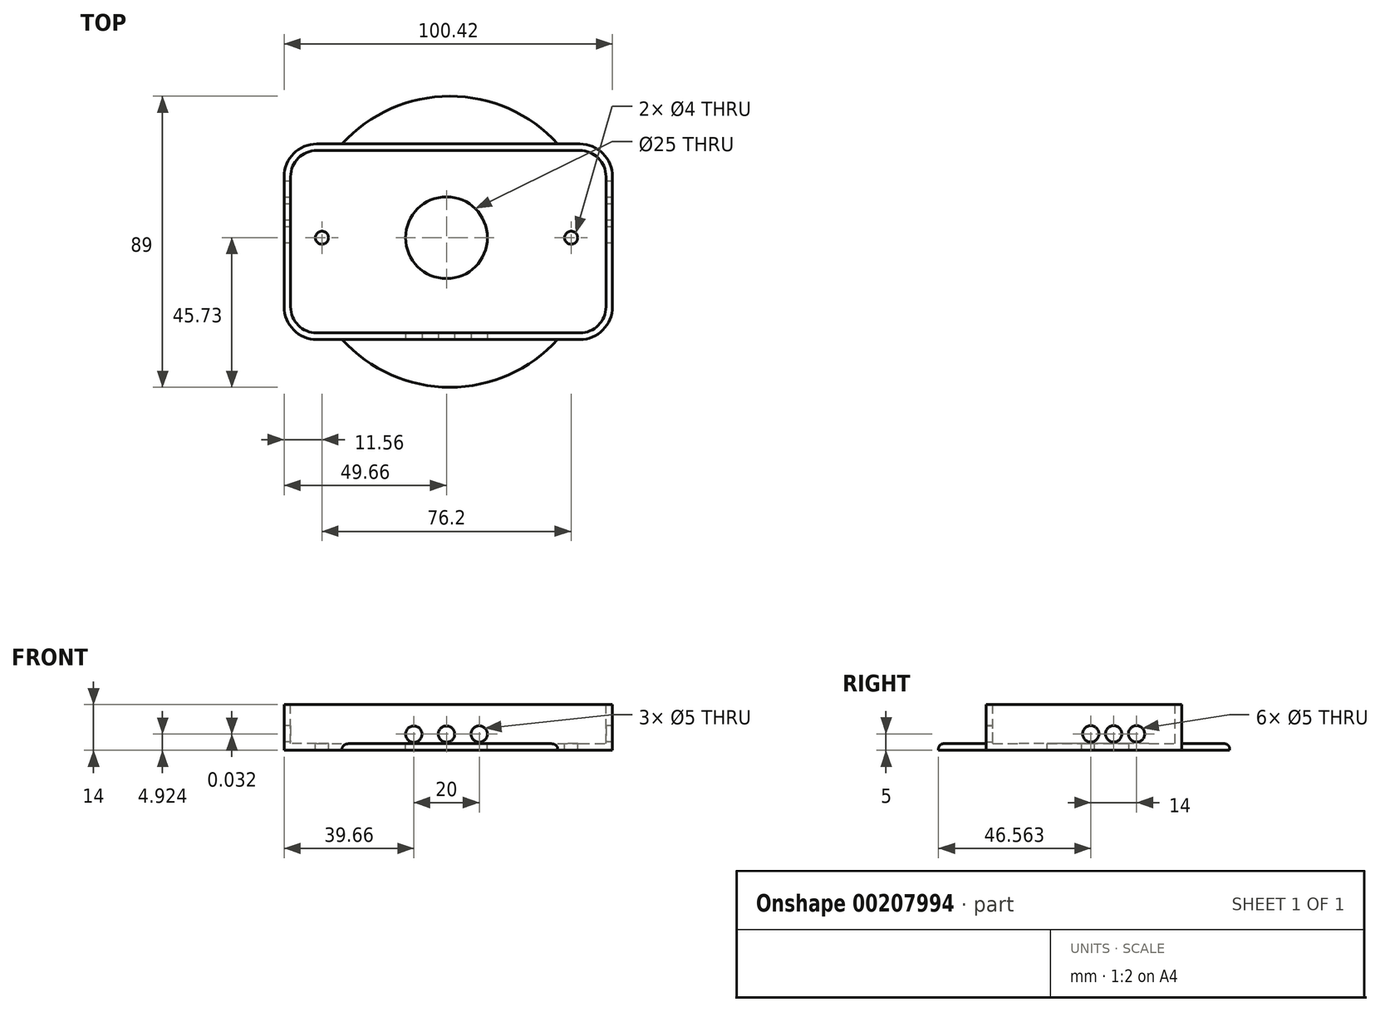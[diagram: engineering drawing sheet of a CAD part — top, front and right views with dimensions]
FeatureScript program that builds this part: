
annotation { "Feature Type Name" : "Feature", "Feature Type Description" : "" }
export const myFeature = defineFeature(function(context is Context, id is Id, definition is map)
    precondition{}
    {
        {
            var Q0;
            Q0=qCreatedBy(makeId("Top.planeOp"),FACE);
            var sketch = newSketch(context, id + "F0", { "sketchPlane" : qUnion([Q0])});
            skCircle(sketch, "E0", {"center": v(-41.26, 20.47) * mm, "radius": 3.2 * mm});
            skCircle(sketch, "E1", {"center": v(37.34, 20.47) * mm, "radius": 3.2 * mm});
            skCircle(sketch, "E2", {"center": v(37.34, -22.93) * mm, "radius": 3.2 * mm});
            skCircle(sketch, "E3", {"center": v(-41.26, -22.93) * mm, "radius": 3.2 * mm});
            skLineSegment(sketch, "E4.bottom", {"start": v(-44.46, 23.67) * mm, "end": v(40.54, 23.67) * mm});
            skLineSegment(sketch, "E4.top", {"start": v(-44.46, -26.13) * mm, "end": v(40.54, -26.13) * mm});
            skLineSegment(sketch, "E4.left", {"start": v(-44.46, 23.67) * mm, "end": v(-44.46, -26.13) * mm});
            skLineSegment(sketch, "E4.right", {"start": v(40.54, 23.67) * mm, "end": v(40.54, -26.13) * mm});
            skLineSegment(sketch, "E5.bottom", {"start": v(-28.76, 21.37) * mm, "end": v(30.84, 21.37) * mm});
            skLineSegment(sketch, "E5.top", {"start": v(-28.76, -23.83) * mm, "end": v(30.84, -23.83) * mm});
            skLineSegment(sketch, "E5.left", {"start": v(-28.76, 21.37) * mm, "end": v(-28.76, -23.83) * mm});
            skLineSegment(sketch, "E5.right", {"start": v(30.84, 21.37) * mm, "end": v(30.84, -23.83) * mm});
            skLineSegment(sketch, "E6.bottom", {"start": v(-39.66, 28.67) * mm, "end": v(40.76, 28.67) * mm});
            skLineSegment(sketch, "E6.top", {"start": v(-39.66, -31.13) * mm, "end": v(40.76, -31.13) * mm});
            skLineSegment(sketch, "E6.left", {"start": v(-49.66, 18.67) * mm, "end": v(-49.66, -21.13) * mm});
            skLineSegment(sketch, "E6.right", {"start": v(50.76, 18.67) * mm, "end": v(50.76, -21.13) * mm});
            skCircle(sketch, "E7", {"center": v(1.04, -1.23) * mm, "radius": 44.5 * mm});
            skPoint(sketch, "E7.centerSnap0", {"position": v(1.04, -23.83) * mm});
            skPoint(sketch, "E7.centerSnap1", {"position": v(-28.76, -1.23) * mm});
            skPoint(sketch, "E8.visualSharp", {"position": v(50.76, 28.67) * mm});
            skArc(sketch, "E8.filletArc", {"start": v(50.76, 18.67) * mm, "mid": v(47.83, 25.74) * mm, "end": v(40.76, 28.67) * mm});
            skPoint(sketch, "E9.visualSharp", {"position": v(-49.66, 28.67) * mm});
            skArc(sketch, "E9.filletArc", {"start": v(-39.66, 28.67) * mm, "mid": v(-46.74, 25.74) * mm, "end": v(-49.66, 18.67) * mm});
            skPoint(sketch, "E10.visualSharp", {"position": v(-49.66, -31.13) * mm});
            skArc(sketch, "E10.filletArc", {"start": v(-49.66, -21.13) * mm, "mid": v(-46.74, -28.2) * mm, "end": v(-39.66, -31.13) * mm});
            skPoint(sketch, "E11.visualSharp", {"position": v(50.76, -31.13) * mm});
            skArc(sketch, "E11.filletArc", {"start": v(40.76, -31.13) * mm, "mid": v(47.83, -28.2) * mm, "end": v(50.76, -21.13) * mm});
            skSolve(sketch);
        }
        {
            var Q0;
            {var subQ1=sQuery(id+"F0.wireOp",EDGE,"E4.bottom");var subQ13=sQuery(id+"F0.wireOp",EDGE,"E0");var subQ20=makeQuery(id+"F0.imprint","INTERSECT",VERTEX,{"disambiguationData":[OD(1.0)],"derivedFrom":[subQ13,subQ1]});Q0=makeQuery(id+"F0.imprint","IMPRINT",FACE,{"disambiguationData":[TD([[makeQuery(id+"F0.imprint","IMPRINT",EDGE,{"disambiguationData":[TD([[subQ20,1.0]])],"derivedFrom":subQ13}),-1.0]])]});}
            var Q1;
            {var subQ0=sQuery(id+"F0.wireOp",EDGE,"E7");var subQ7=sQuery(id+"F0.wireOp",EDGE,"E5.bottom");var subQ12=makeQuery(id+"F0.imprint","INTERSECT",VERTEX,{"disambiguationData":[OD(0.0)],"derivedFrom":[subQ7,subQ0]});Q1=makeQuery(id+"F0.imprint","IMPRINT",FACE,{"disambiguationData":[TD([[makeQuery(id+"F0.imprint","IMPRINT",EDGE,{"disambiguationData":[TD([[subQ12,-1.0]])],"derivedFrom":subQ7}),-1.0]])]});}
            var Q2;
            {var subQ0=sQuery(id+"F0.wireOp",EDGE,"E4.bottom");var subQ1=sQuery(id+"F0.wireOp",EDGE,"E1");var subQ2=makeQuery(id+"F0.imprint","INTERSECT",VERTEX,{"disambiguationData":[OD(0.0)],"derivedFrom":[subQ1,subQ0]});Q2=makeQuery(id+"F0.imprint","IMPRINT",FACE,{"disambiguationData":[TD([[makeQuery(id+"F0.imprint","IMPRINT",EDGE,{"disambiguationData":[TD([[subQ2,1.0]])],"derivedFrom":subQ1}),1.0]])]});}
            var Q3;
            {var subQ0=sQuery(id+"F0.wireOp",EDGE,"E4.left");var subQ1=sQuery(id+"F0.wireOp",EDGE,"E3");var subQ2=makeQuery(id+"F0.imprint","INTERSECT",VERTEX,{"disambiguationData":[OD(0.0)],"derivedFrom":[subQ1,subQ0]});Q3=makeQuery(id+"F0.imprint","IMPRINT",FACE,{"disambiguationData":[TD([[makeQuery(id+"F0.imprint","IMPRINT",EDGE,{"disambiguationData":[TD([[subQ2,-1.0]])],"derivedFrom":subQ1}),1.0]])]});}
            var Q4;
            {var subQ0=sQuery(id+"F0.wireOp",EDGE,"E7");var subQ1=sQuery(id+"F0.wireOp",EDGE,"E4.top");var subQ2=makeQuery(id+"F0.imprint","INTERSECT",VERTEX,{"disambiguationData":[OD(0.0)],"derivedFrom":[subQ1,subQ0]});Q4=makeQuery(id+"F0.imprint","IMPRINT",FACE,{"disambiguationData":[TD([[makeQuery(id+"F0.imprint","IMPRINT",EDGE,{"disambiguationData":[TD([[subQ2,-1.0]])],"derivedFrom":subQ1}),-1.0]])]});}
            var Q5;
            {var subQ0=sQuery(id+"F0.wireOp",EDGE,"E7");var subQ1=sQuery(id+"F0.wireOp",EDGE,"E4.top");var subQ2=makeQuery(id+"F0.imprint","INTERSECT",VERTEX,{"disambiguationData":[OD(0.0)],"derivedFrom":[subQ1,subQ0]});Q5=makeQuery(id+"F0.imprint","IMPRINT",FACE,{"disambiguationData":[TD([[makeQuery(id+"F0.imprint","IMPRINT",EDGE,{"disambiguationData":[TD([[subQ2,-1.0]])],"derivedFrom":subQ1}),1.0]])]});}
            var Q6;
            {var subQ0=sQuery(id+"F0.wireOp",EDGE,"E7");var subQ1=sQuery(id+"F0.wireOp",EDGE,"E6.top");var subQ2=makeQuery(id+"F0.imprint","INTERSECT",VERTEX,{"disambiguationData":[OD(0.0)],"derivedFrom":[subQ1,subQ0]});Q6=makeQuery(id+"F0.imprint","IMPRINT",FACE,{"disambiguationData":[TD([[makeQuery(id+"F0.imprint","IMPRINT",EDGE,{"disambiguationData":[TD([[subQ2,-1.0]])],"derivedFrom":subQ1}),-1.0]])]});}
            var Q7;
            {var subQ0=sQuery(id+"F0.wireOp",EDGE,"E7");var subQ1=sQuery(id+"F0.wireOp",EDGE,"E6.bottom");var subQ2=makeQuery(id+"F0.imprint","INTERSECT",VERTEX,{"disambiguationData":[OD(0.0)],"derivedFrom":[subQ1,subQ0]});Q7=makeQuery(id+"F0.imprint","IMPRINT",FACE,{"disambiguationData":[TD([[makeQuery(id+"F0.imprint","IMPRINT",EDGE,{"disambiguationData":[TD([[subQ2,-1.0]])],"derivedFrom":subQ1}),1.0]])]});}
            var Q8;
            Q8=makeQuery(id+"F0.imprint","IMPRINT",FACE,{"disambiguationData":[TD([[makeQuery(id+"F0.imprint","IMPRINT",EDGE,{"derivedFrom":sQuery(id+"F0.wireOp",EDGE,"E6.right")}),-1.0]])]});
            var Q9;
            {var subQ1=sQuery(id+"F0.wireOp",EDGE,"E4.bottom");var subQ5=sQuery(id+"F0.wireOp",EDGE,"E1");var subQ6=makeQuery(id+"F0.imprint","INTERSECT",VERTEX,{"disambiguationData":[OD(1.0)],"derivedFrom":[subQ5,subQ1]});Q9=makeQuery(id+"F0.imprint","IMPRINT",FACE,{"disambiguationData":[TD([[makeQuery(id+"F0.imprint","IMPRINT",EDGE,{"disambiguationData":[TD([[subQ6,-1.0]])],"derivedFrom":subQ5}),-1.0]])]});}
            var Q10;
            {var subQ0=sQuery(id+"F0.wireOp",EDGE,"E4.bottom");var subQ1=sQuery(id+"F0.wireOp",EDGE,"E0");var subQ2=makeQuery(id+"F0.imprint","INTERSECT",VERTEX,{"disambiguationData":[OD(0.0)],"derivedFrom":[subQ1,subQ0]});Q10=makeQuery(id+"F0.imprint","IMPRINT",FACE,{"disambiguationData":[TD([[makeQuery(id+"F0.imprint","IMPRINT",EDGE,{"disambiguationData":[TD([[subQ2,-1.0]])],"derivedFrom":subQ1}),1.0]])]});}
            var Q11;
            {var subQ0=sQuery(id+"F0.wireOp",EDGE,"E7");var subQ1=sQuery(id+"F0.wireOp",EDGE,"E4.bottom");var subQ2=makeQuery(id+"F0.imprint","INTERSECT",VERTEX,{"disambiguationData":[OD(0.0)],"derivedFrom":[subQ1,subQ0]});Q11=makeQuery(id+"F0.imprint","IMPRINT",FACE,{"disambiguationData":[TD([[makeQuery(id+"F0.imprint","IMPRINT",EDGE,{"disambiguationData":[TD([[subQ2,-1.0]])],"derivedFrom":subQ1}),-1.0]])]});}
            var Q12;
            {var subQ0=sQuery(id+"F0.wireOp",EDGE,"E7");var subQ1=sQuery(id+"F0.wireOp",EDGE,"E5.left");var subQ2=makeQuery(id+"F0.imprint","INTERSECT",VERTEX,{"disambiguationData":[OD(0.0)],"derivedFrom":[subQ1,subQ0]});Q12=makeQuery(id+"F0.imprint","IMPRINT",FACE,{"disambiguationData":[TD([[makeQuery(id+"F0.imprint","IMPRINT",EDGE,{"disambiguationData":[TD([[subQ2,-1.0]])],"derivedFrom":subQ1}),-1.0]])]});}
            var Q13;
            Q13=makeQuery(id+"F0.imprint","IMPRINT",FACE,{"disambiguationData":[TD([[makeQuery(id+"F0.imprint","IMPRINT",EDGE,{"derivedFrom":sQuery(id+"F0.wireOp",EDGE,"E6.left")}),1.0]])]});
            var Q14;
            {var subQ0=sQuery(id+"F0.wireOp",EDGE,"E4.top");var subQ1=sQuery(id+"F0.wireOp",EDGE,"E2");var subQ2=makeQuery(id+"F0.imprint","INTERSECT",VERTEX,{"disambiguationData":[OD(0.0)],"derivedFrom":[subQ1,subQ0]});Q14=makeQuery(id+"F0.imprint","IMPRINT",FACE,{"disambiguationData":[TD([[makeQuery(id+"F0.imprint","IMPRINT",EDGE,{"disambiguationData":[TD([[subQ2,1.0]])],"derivedFrom":subQ1}),1.0]])]});}
            var Q15;
            {var subQ0=sQuery(id+"F0.wireOp",EDGE,"E7");var subQ1=sQuery(id+"F0.wireOp",EDGE,"E5.right");var subQ2=makeQuery(id+"F0.imprint","INTERSECT",VERTEX,{"disambiguationData":[OD(0.0)],"derivedFrom":[subQ1,subQ0]});Q15=makeQuery(id+"F0.imprint","IMPRINT",FACE,{"disambiguationData":[TD([[makeQuery(id+"F0.imprint","IMPRINT",EDGE,{"disambiguationData":[TD([[subQ2,-1.0]])],"derivedFrom":subQ1}),1.0]])]});}
            var Q16;
            {var subQ0=sQuery(id+"F0.wireOp",EDGE,"E7");var subQ1=sQuery(id+"F0.wireOp",EDGE,"E4.bottom");var subQ2=makeQuery(id+"F0.imprint","INTERSECT",VERTEX,{"disambiguationData":[OD(0.0)],"derivedFrom":[subQ1,subQ0]});Q16=makeQuery(id+"F0.imprint","IMPRINT",FACE,{"disambiguationData":[TD([[makeQuery(id+"F0.imprint","IMPRINT",EDGE,{"disambiguationData":[TD([[subQ2,-1.0]])],"derivedFrom":subQ1}),1.0]])]});}
            var Q17;
            {var subQ0=sQuery(id+"F0.wireOp",EDGE,"E5.right");var subQ1=sQuery(id+"F0.wireOp",EDGE,"E5.top");var subQ2=makeQuery(id+"F0.imprint","INTERSECT",VERTEX,{"derivedFrom":[subQ1,subQ0]});Q17=makeQuery(id+"F0.imprint","IMPRINT",FACE,{"disambiguationData":[TD([[makeQuery(id+"F0.imprint","IMPRINT",EDGE,{"disambiguationData":[TD([[subQ2,1.0]])],"derivedFrom":subQ1}),1.0]])]});}
            var Q18;
            {var subQ0=sQuery(id+"F0.wireOp",EDGE,"E4.left");var subQ1=sQuery(id+"F0.wireOp",EDGE,"E3");var subQ2=makeQuery(id+"F0.imprint","INTERSECT",VERTEX,{"disambiguationData":[OD(0.0)],"derivedFrom":[subQ1,subQ0]});Q18=makeQuery(id+"F0.imprint","IMPRINT",FACE,{"disambiguationData":[TD([[makeQuery(id+"F0.imprint","IMPRINT",EDGE,{"disambiguationData":[TD([[subQ2,1.0]])],"derivedFrom":subQ1}),1.0]])]});}
            var Q19;
            {var subQ0=sQuery(id+"F0.wireOp",EDGE,"E4.left");var subQ1=sQuery(id+"F0.wireOp",EDGE,"E3");var subQ2=makeQuery(id+"F0.imprint","INTERSECT",VERTEX,{"disambiguationData":[OD(0.0)],"derivedFrom":[subQ1,subQ0]});Q19=makeQuery(id+"F0.imprint","IMPRINT",FACE,{"disambiguationData":[TD([[makeQuery(id+"F0.imprint","IMPRINT",EDGE,{"disambiguationData":[TD([[subQ2,-1.0]])],"derivedFrom":subQ1}),-1.0]])]});}
            var Q20;
            {var subQ0=sQuery(id+"F0.wireOp",EDGE,"E4.right");var subQ1=sQuery(id+"F0.wireOp",EDGE,"E2");var subQ2=makeQuery(id+"F0.imprint","INTERSECT",VERTEX,{"disambiguationData":[OD(0.0)],"derivedFrom":[subQ1,subQ0]});Q20=makeQuery(id+"F0.imprint","IMPRINT",FACE,{"disambiguationData":[TD([[makeQuery(id+"F0.imprint","IMPRINT",EDGE,{"disambiguationData":[TD([[subQ2,1.0]])],"derivedFrom":subQ1}),1.0]])]});}
            var Q21;
            {var subQ0=sQuery(id+"F0.wireOp",EDGE,"E4.top");var subQ1=sQuery(id+"F0.wireOp",EDGE,"E2");var subQ2=makeQuery(id+"F0.imprint","INTERSECT",VERTEX,{"disambiguationData":[OD(1.0)],"derivedFrom":[subQ1,subQ0]});Q21=makeQuery(id+"F0.imprint","IMPRINT",FACE,{"disambiguationData":[TD([[makeQuery(id+"F0.imprint","IMPRINT",EDGE,{"disambiguationData":[TD([[subQ2,-1.0]])],"derivedFrom":subQ1}),-1.0]])]});}
            var Q22;
            {var subQ0=sQuery(id+"F0.wireOp",EDGE,"E4.top");var subQ1=sQuery(id+"F0.wireOp",EDGE,"E2");var subQ2=makeQuery(id+"F0.imprint","INTERSECT",VERTEX,{"disambiguationData":[OD(0.0)],"derivedFrom":[subQ1,subQ0]});Q22=makeQuery(id+"F0.imprint","IMPRINT",FACE,{"disambiguationData":[TD([[makeQuery(id+"F0.imprint","IMPRINT",EDGE,{"disambiguationData":[TD([[subQ2,-1.0]])],"derivedFrom":subQ1}),1.0]])]});}
            var Q23;
            {var subQ0=sQuery(id+"F0.wireOp",EDGE,"E4.bottom");var subQ1=sQuery(id+"F0.wireOp",EDGE,"E1");var subQ2=makeQuery(id+"F0.imprint","INTERSECT",VERTEX,{"disambiguationData":[OD(0.0)],"derivedFrom":[subQ1,subQ0]});Q23=makeQuery(id+"F0.imprint","IMPRINT",FACE,{"disambiguationData":[TD([[makeQuery(id+"F0.imprint","IMPRINT",EDGE,{"disambiguationData":[TD([[subQ2,-1.0]])],"derivedFrom":subQ1}),1.0]])]});}
            var Q24;
            {var subQ0=sQuery(id+"F0.wireOp",EDGE,"E4.right");var subQ1=sQuery(id+"F0.wireOp",EDGE,"E1");var subQ2=makeQuery(id+"F0.imprint","INTERSECT",VERTEX,{"disambiguationData":[OD(0.0)],"derivedFrom":[subQ1,subQ0]});Q24=makeQuery(id+"F0.imprint","IMPRINT",FACE,{"disambiguationData":[TD([[makeQuery(id+"F0.imprint","IMPRINT",EDGE,{"disambiguationData":[TD([[subQ2,1.0]])],"derivedFrom":subQ1}),1.0]])]});}
            var Q25;
            {var subQ0=sQuery(id+"F0.wireOp",EDGE,"E4.bottom");var subQ1=sQuery(id+"F0.wireOp",EDGE,"E1");var subQ2=makeQuery(id+"F0.imprint","INTERSECT",VERTEX,{"disambiguationData":[OD(0.0)],"derivedFrom":[subQ1,subQ0]});Q25=makeQuery(id+"F0.imprint","IMPRINT",FACE,{"disambiguationData":[TD([[makeQuery(id+"F0.imprint","IMPRINT",EDGE,{"disambiguationData":[TD([[subQ2,1.0]])],"derivedFrom":subQ1}),-1.0]])]});}
            var Q26;
            {var subQ0=sQuery(id+"F0.wireOp",EDGE,"E4.left");var subQ1=sQuery(id+"F0.wireOp",EDGE,"E0");var subQ2=makeQuery(id+"F0.imprint","INTERSECT",VERTEX,{"disambiguationData":[OD(0.0)],"derivedFrom":[subQ1,subQ0]});Q26=makeQuery(id+"F0.imprint","IMPRINT",FACE,{"disambiguationData":[TD([[makeQuery(id+"F0.imprint","IMPRINT",EDGE,{"disambiguationData":[TD([[subQ2,-1.0]])],"derivedFrom":subQ1}),1.0]])]});}
            var Q27;
            {var subQ0=sQuery(id+"F0.wireOp",EDGE,"E4.bottom");var subQ1=sQuery(id+"F0.wireOp",EDGE,"E0");var subQ2=makeQuery(id+"F0.imprint","INTERSECT",VERTEX,{"disambiguationData":[OD(0.0)],"derivedFrom":[subQ1,subQ0]});Q27=makeQuery(id+"F0.imprint","IMPRINT",FACE,{"disambiguationData":[TD([[makeQuery(id+"F0.imprint","IMPRINT",EDGE,{"disambiguationData":[TD([[subQ2,-1.0]])],"derivedFrom":subQ1}),-1.0]])]});}
            var Q28;
            {var subQ0=sQuery(id+"F0.wireOp",EDGE,"E4.bottom");var subQ1=sQuery(id+"F0.wireOp",EDGE,"E0");var subQ2=makeQuery(id+"F0.imprint","INTERSECT",VERTEX,{"disambiguationData":[OD(0.0)],"derivedFrom":[subQ1,subQ0]});Q28=makeQuery(id+"F0.imprint","IMPRINT",FACE,{"disambiguationData":[TD([[makeQuery(id+"F0.imprint","IMPRINT",EDGE,{"disambiguationData":[TD([[subQ2,1.0]])],"derivedFrom":subQ1}),1.0]])]});}
            var Q29;
            {var subQ0=sQuery(id+"F0.wireOp",EDGE,"E5.left");var subQ1=sQuery(id+"F0.wireOp",EDGE,"E5.top");var subQ2=makeQuery(id+"F0.imprint","INTERSECT",VERTEX,{"derivedFrom":[subQ1,subQ0]});Q29=makeQuery(id+"F0.imprint","IMPRINT",FACE,{"disambiguationData":[TD([[makeQuery(id+"F0.imprint","IMPRINT",EDGE,{"disambiguationData":[TD([[subQ2,-1.0]])],"derivedFrom":subQ1}),1.0]])]});}
            var Q30;
            {var subQ0=sQuery(id+"F0.wireOp",EDGE,"E5.left");var subQ1=sQuery(id+"F0.wireOp",EDGE,"E5.bottom");var subQ2=makeQuery(id+"F0.imprint","INTERSECT",VERTEX,{"derivedFrom":[subQ1,subQ0]});Q30=makeQuery(id+"F0.imprint","IMPRINT",FACE,{"disambiguationData":[TD([[makeQuery(id+"F0.imprint","IMPRINT",EDGE,{"disambiguationData":[TD([[subQ2,-1.0]])],"derivedFrom":subQ1}),-1.0]])]});}
            var Q31;
            {var subQ0=sQuery(id+"F0.wireOp",EDGE,"E4.top");var subQ1=sQuery(id+"F0.wireOp",EDGE,"E3");var subQ2=makeQuery(id+"F0.imprint","INTERSECT",VERTEX,{"disambiguationData":[OD(0.0)],"derivedFrom":[subQ1,subQ0]});Q31=makeQuery(id+"F0.imprint","IMPRINT",FACE,{"disambiguationData":[TD([[makeQuery(id+"F0.imprint","IMPRINT",EDGE,{"disambiguationData":[TD([[subQ2,-1.0]])],"derivedFrom":subQ1}),1.0]])]});}
            var Q32;
            {var subQ0=sQuery(id+"F0.wireOp",EDGE,"E5.right");var subQ1=sQuery(id+"F0.wireOp",EDGE,"E5.bottom");var subQ2=makeQuery(id+"F0.imprint","INTERSECT",VERTEX,{"derivedFrom":[subQ1,subQ0]});Q32=makeQuery(id+"F0.imprint","IMPRINT",FACE,{"disambiguationData":[TD([[makeQuery(id+"F0.imprint","IMPRINT",EDGE,{"disambiguationData":[TD([[subQ2,1.0]])],"derivedFrom":subQ1}),-1.0]])]});}
            var Q33;
            {var subQ0=sQuery(id+"F0.wireOp",EDGE,"E4.left");var subQ1=sQuery(id+"F0.wireOp",EDGE,"E0");var subQ2=makeQuery(id+"F0.imprint","INTERSECT",VERTEX,{"derivedFrom":[subQ1,subQ0]});Q33=makeQuery(id+"F0.imprint","IMPRINT",FACE,{"disambiguationData":[TD([[makeQuery(id+"F0.imprint","IMPRINT",EDGE,{"disambiguationData":[TD([[subQ2,-1.0]])],"derivedFrom":subQ1}),-1.0]])]});}
            var Q34;
            {var subQ0=sQuery(id+"F0.wireOp",EDGE,"E7");var subQ1=sQuery(id+"F0.wireOp",EDGE,"E3");var subQ2=makeQuery(id+"F0.imprint","INTERSECT",VERTEX,{"disambiguationData":[OD(1.0)],"derivedFrom":[subQ1,subQ0]});Q34=makeQuery(id+"F0.imprint","IMPRINT",FACE,{"disambiguationData":[TD([[makeQuery(id+"F0.imprint","IMPRINT",EDGE,{"disambiguationData":[TD([[subQ2,1.0]])],"derivedFrom":subQ1}),-1.0]])]});}
            var Q35;
            {var subQ0=sQuery(id+"F0.wireOp",EDGE,"E4.right");var subQ1=sQuery(id+"F0.wireOp",EDGE,"E2");var subQ2=makeQuery(id+"F0.imprint","INTERSECT",VERTEX,{"derivedFrom":[subQ1,subQ0]});Q35=makeQuery(id+"F0.imprint","IMPRINT",FACE,{"disambiguationData":[TD([[makeQuery(id+"F0.imprint","IMPRINT",EDGE,{"disambiguationData":[TD([[subQ2,1.0]])],"derivedFrom":subQ1}),-1.0]])]});}
            var Q36;
            {var subQ0=sQuery(id+"F0.wireOp",EDGE,"E7");var subQ1=sQuery(id+"F0.wireOp",EDGE,"E4.right");var subQ2=makeQuery(id+"F0.imprint","INTERSECT",VERTEX,{"disambiguationData":[OD(0.0)],"derivedFrom":[subQ1,subQ0]});Q36=makeQuery(id+"F0.imprint","IMPRINT",FACE,{"disambiguationData":[TD([[makeQuery(id+"F0.imprint","IMPRINT",EDGE,{"disambiguationData":[TD([[subQ2,-1.0]])],"derivedFrom":subQ1}),1.0]])]});}
            var Q37;
            {var subQ0=sQuery(id+"F0.wireOp",EDGE,"E7");var subQ1=sQuery(id+"F0.wireOp",EDGE,"E1");var subQ2=makeQuery(id+"F0.imprint","INTERSECT",VERTEX,{"disambiguationData":[OD(0.0)],"derivedFrom":[subQ1,subQ0]});Q37=makeQuery(id+"F0.imprint","IMPRINT",FACE,{"disambiguationData":[TD([[makeQuery(id+"F0.imprint","IMPRINT",EDGE,{"disambiguationData":[TD([[subQ2,1.0]])],"derivedFrom":subQ1}),-1.0]])]});}
            var Q38;
            {var subQ0=sQuery(id+"F0.wireOp",EDGE,"E7");var subQ1=sQuery(id+"F0.wireOp",EDGE,"E0");var subQ2=makeQuery(id+"F0.imprint","INTERSECT",VERTEX,{"disambiguationData":[OD(0.0)],"derivedFrom":[subQ1,subQ0]});Q38=makeQuery(id+"F0.imprint","IMPRINT",FACE,{"disambiguationData":[TD([[makeQuery(id+"F0.imprint","IMPRINT",EDGE,{"disambiguationData":[TD([[subQ2,-1.0]])],"derivedFrom":subQ1}),1.0]])]});}
            var Q39;
            {var subQ0=sQuery(id+"F0.wireOp",EDGE,"E7");var subQ1=sQuery(id+"F0.wireOp",EDGE,"E3");var subQ2=makeQuery(id+"F0.imprint","INTERSECT",VERTEX,{"disambiguationData":[OD(0.0)],"derivedFrom":[subQ1,subQ0]});Q39=makeQuery(id+"F0.imprint","IMPRINT",FACE,{"disambiguationData":[TD([[makeQuery(id+"F0.imprint","IMPRINT",EDGE,{"disambiguationData":[TD([[subQ2,1.0]])],"derivedFrom":subQ1}),1.0]])]});}
            var Q40;
            {var subQ0=sQuery(id+"F0.wireOp",EDGE,"E7");var subQ1=sQuery(id+"F0.wireOp",EDGE,"E2");var subQ2=makeQuery(id+"F0.imprint","INTERSECT",VERTEX,{"disambiguationData":[OD(0.0)],"derivedFrom":[subQ1,subQ0]});Q40=makeQuery(id+"F0.imprint","IMPRINT",FACE,{"disambiguationData":[TD([[makeQuery(id+"F0.imprint","IMPRINT",EDGE,{"disambiguationData":[TD([[subQ2,1.0]])],"derivedFrom":subQ1}),-1.0]])]});}
            var Q41;
            {var subQ0=sQuery(id+"F0.wireOp",EDGE,"E4.right");var subQ1=sQuery(id+"F0.wireOp",EDGE,"E1");var subQ2=makeQuery(id+"F0.imprint","INTERSECT",VERTEX,{"derivedFrom":[subQ1,subQ0]});Q41=makeQuery(id+"F0.imprint","IMPRINT",FACE,{"disambiguationData":[TD([[makeQuery(id+"F0.imprint","IMPRINT",EDGE,{"disambiguationData":[TD([[subQ2,1.0]])],"derivedFrom":subQ1}),-1.0]])]});}
            extrude(context, id + "F1", {"entities" : qUnion([Q0, Q1, Q2, Q3, Q4, Q5, Q6, Q7, Q8, Q9, Q10, Q11, Q12, Q13, Q14, Q15, Q16, Q17, Q18, Q19, Q20, Q21, Q22, Q23, Q24, Q25, Q26, Q27, Q28, Q29, Q30, Q31, Q32, Q33, Q34, Q35, Q36, Q37, Q38, Q39, Q40, Q41]), "oppositeDirection" : true, "depth" : 2 * mm});
        }
        {
            var Q0;
            Q0=makeQuery(id+"F0.imprint","IMPRINT",FACE,{"disambiguationData":[TD([[makeQuery(id+"F0.imprint","IMPRINT",EDGE,{"derivedFrom":sQuery(id+"F0.wireOp",EDGE,"E6.left")}),1.0]])]});
            var Q1;
            {var subQ0=sQuery(id+"F0.wireOp",EDGE,"E7");var subQ1=sQuery(id+"F0.wireOp",EDGE,"E4.bottom");var subQ2=makeQuery(id+"F0.imprint","INTERSECT",VERTEX,{"disambiguationData":[OD(0.0)],"derivedFrom":[subQ1,subQ0]});Q1=makeQuery(id+"F0.imprint","IMPRINT",FACE,{"disambiguationData":[TD([[makeQuery(id+"F0.imprint","IMPRINT",EDGE,{"disambiguationData":[TD([[subQ2,-1.0]])],"derivedFrom":subQ1}),1.0]])]});}
            var Q2;
            {var subQ1=sQuery(id+"F0.wireOp",EDGE,"E4.bottom");var subQ5=sQuery(id+"F0.wireOp",EDGE,"E1");var subQ6=makeQuery(id+"F0.imprint","INTERSECT",VERTEX,{"disambiguationData":[OD(1.0)],"derivedFrom":[subQ5,subQ1]});Q2=makeQuery(id+"F0.imprint","IMPRINT",FACE,{"disambiguationData":[TD([[makeQuery(id+"F0.imprint","IMPRINT",EDGE,{"disambiguationData":[TD([[subQ6,-1.0]])],"derivedFrom":subQ5}),-1.0]])]});}
            var Q3;
            {var subQ0=sQuery(id+"F0.wireOp",EDGE,"E4.bottom");var subQ1=sQuery(id+"F0.wireOp",EDGE,"E1");var subQ2=makeQuery(id+"F0.imprint","INTERSECT",VERTEX,{"disambiguationData":[OD(0.0)],"derivedFrom":[subQ1,subQ0]});Q3=makeQuery(id+"F0.imprint","IMPRINT",FACE,{"disambiguationData":[TD([[makeQuery(id+"F0.imprint","IMPRINT",EDGE,{"disambiguationData":[TD([[subQ2,1.0]])],"derivedFrom":subQ1}),1.0]])]});}
            var Q4;
            {var subQ0=sQuery(id+"F0.wireOp",EDGE,"E4.top");var subQ1=sQuery(id+"F0.wireOp",EDGE,"E2");var subQ2=makeQuery(id+"F0.imprint","INTERSECT",VERTEX,{"disambiguationData":[OD(0.0)],"derivedFrom":[subQ1,subQ0]});Q4=makeQuery(id+"F0.imprint","IMPRINT",FACE,{"disambiguationData":[TD([[makeQuery(id+"F0.imprint","IMPRINT",EDGE,{"disambiguationData":[TD([[subQ2,1.0]])],"derivedFrom":subQ1}),1.0]])]});}
            var Q5;
            {var subQ0=sQuery(id+"F0.wireOp",EDGE,"E7");var subQ1=sQuery(id+"F0.wireOp",EDGE,"E5.right");var subQ2=makeQuery(id+"F0.imprint","INTERSECT",VERTEX,{"disambiguationData":[OD(0.0)],"derivedFrom":[subQ1,subQ0]});Q5=makeQuery(id+"F0.imprint","IMPRINT",FACE,{"disambiguationData":[TD([[makeQuery(id+"F0.imprint","IMPRINT",EDGE,{"disambiguationData":[TD([[subQ2,-1.0]])],"derivedFrom":subQ1}),1.0]])]});}
            var Q6;
            {var subQ0=sQuery(id+"F0.wireOp",EDGE,"E7");var subQ7=sQuery(id+"F0.wireOp",EDGE,"E5.bottom");var subQ12=makeQuery(id+"F0.imprint","INTERSECT",VERTEX,{"disambiguationData":[OD(0.0)],"derivedFrom":[subQ7,subQ0]});Q6=makeQuery(id+"F0.imprint","IMPRINT",FACE,{"disambiguationData":[TD([[makeQuery(id+"F0.imprint","IMPRINT",EDGE,{"disambiguationData":[TD([[subQ12,-1.0]])],"derivedFrom":subQ7}),-1.0]])]});}
            var Q7;
            {var subQ0=sQuery(id+"F0.wireOp",EDGE,"E7");var subQ1=sQuery(id+"F0.wireOp",EDGE,"E4.bottom");var subQ2=makeQuery(id+"F0.imprint","INTERSECT",VERTEX,{"disambiguationData":[OD(0.0)],"derivedFrom":[subQ1,subQ0]});Q7=makeQuery(id+"F0.imprint","IMPRINT",FACE,{"disambiguationData":[TD([[makeQuery(id+"F0.imprint","IMPRINT",EDGE,{"disambiguationData":[TD([[subQ2,-1.0]])],"derivedFrom":subQ1}),-1.0]])]});}
            var Q8;
            {var subQ0=sQuery(id+"F0.wireOp",EDGE,"E7");var subQ1=sQuery(id+"F0.wireOp",EDGE,"E4.top");var subQ2=makeQuery(id+"F0.imprint","INTERSECT",VERTEX,{"disambiguationData":[OD(0.0)],"derivedFrom":[subQ1,subQ0]});Q8=makeQuery(id+"F0.imprint","IMPRINT",FACE,{"disambiguationData":[TD([[makeQuery(id+"F0.imprint","IMPRINT",EDGE,{"disambiguationData":[TD([[subQ2,-1.0]])],"derivedFrom":subQ1}),1.0]])]});}
            var Q9;
            {var subQ1=sQuery(id+"F0.wireOp",EDGE,"E4.bottom");var subQ13=sQuery(id+"F0.wireOp",EDGE,"E0");var subQ20=makeQuery(id+"F0.imprint","INTERSECT",VERTEX,{"disambiguationData":[OD(1.0)],"derivedFrom":[subQ13,subQ1]});Q9=makeQuery(id+"F0.imprint","IMPRINT",FACE,{"disambiguationData":[TD([[makeQuery(id+"F0.imprint","IMPRINT",EDGE,{"disambiguationData":[TD([[subQ20,1.0]])],"derivedFrom":subQ13}),-1.0]])]});}
            var Q10;
            {var subQ0=sQuery(id+"F0.wireOp",EDGE,"E4.left");var subQ1=sQuery(id+"F0.wireOp",EDGE,"E3");var subQ2=makeQuery(id+"F0.imprint","INTERSECT",VERTEX,{"disambiguationData":[OD(0.0)],"derivedFrom":[subQ1,subQ0]});Q10=makeQuery(id+"F0.imprint","IMPRINT",FACE,{"disambiguationData":[TD([[makeQuery(id+"F0.imprint","IMPRINT",EDGE,{"disambiguationData":[TD([[subQ2,-1.0]])],"derivedFrom":subQ1}),1.0]])]});}
            var Q11;
            {var subQ0=sQuery(id+"F0.wireOp",EDGE,"E4.bottom");var subQ1=sQuery(id+"F0.wireOp",EDGE,"E0");var subQ2=makeQuery(id+"F0.imprint","INTERSECT",VERTEX,{"disambiguationData":[OD(0.0)],"derivedFrom":[subQ1,subQ0]});Q11=makeQuery(id+"F0.imprint","IMPRINT",FACE,{"disambiguationData":[TD([[makeQuery(id+"F0.imprint","IMPRINT",EDGE,{"disambiguationData":[TD([[subQ2,-1.0]])],"derivedFrom":subQ1}),1.0]])]});}
            var Q12;
            {var subQ0=sQuery(id+"F0.wireOp",EDGE,"E4.bottom");var subQ1=sQuery(id+"F0.wireOp",EDGE,"E0");var subQ2=makeQuery(id+"F0.imprint","INTERSECT",VERTEX,{"disambiguationData":[OD(0.0)],"derivedFrom":[subQ1,subQ0]});Q12=makeQuery(id+"F0.imprint","IMPRINT",FACE,{"disambiguationData":[TD([[makeQuery(id+"F0.imprint","IMPRINT",EDGE,{"disambiguationData":[TD([[subQ2,-1.0]])],"derivedFrom":subQ1}),-1.0]])]});}
            var Q13;
            {var subQ0=sQuery(id+"F0.wireOp",EDGE,"E5.left");var subQ1=sQuery(id+"F0.wireOp",EDGE,"E5.bottom");var subQ2=makeQuery(id+"F0.imprint","INTERSECT",VERTEX,{"derivedFrom":[subQ1,subQ0]});Q13=makeQuery(id+"F0.imprint","IMPRINT",FACE,{"disambiguationData":[TD([[makeQuery(id+"F0.imprint","IMPRINT",EDGE,{"disambiguationData":[TD([[subQ2,-1.0]])],"derivedFrom":subQ1}),-1.0]])]});}
            var Q14;
            {var subQ0=sQuery(id+"F0.wireOp",EDGE,"E4.left");var subQ1=sQuery(id+"F0.wireOp",EDGE,"E3");var subQ2=makeQuery(id+"F0.imprint","INTERSECT",VERTEX,{"disambiguationData":[OD(0.0)],"derivedFrom":[subQ1,subQ0]});Q14=makeQuery(id+"F0.imprint","IMPRINT",FACE,{"disambiguationData":[TD([[makeQuery(id+"F0.imprint","IMPRINT",EDGE,{"disambiguationData":[TD([[subQ2,-1.0]])],"derivedFrom":subQ1}),-1.0]])]});}
            var Q15;
            {var subQ0=sQuery(id+"F0.wireOp",EDGE,"E5.left");var subQ1=sQuery(id+"F0.wireOp",EDGE,"E5.top");var subQ2=makeQuery(id+"F0.imprint","INTERSECT",VERTEX,{"derivedFrom":[subQ1,subQ0]});Q15=makeQuery(id+"F0.imprint","IMPRINT",FACE,{"disambiguationData":[TD([[makeQuery(id+"F0.imprint","IMPRINT",EDGE,{"disambiguationData":[TD([[subQ2,-1.0]])],"derivedFrom":subQ1}),1.0]])]});}
            var Q16;
            {var subQ0=sQuery(id+"F0.wireOp",EDGE,"E5.right");var subQ1=sQuery(id+"F0.wireOp",EDGE,"E5.bottom");var subQ2=makeQuery(id+"F0.imprint","INTERSECT",VERTEX,{"derivedFrom":[subQ1,subQ0]});Q16=makeQuery(id+"F0.imprint","IMPRINT",FACE,{"disambiguationData":[TD([[makeQuery(id+"F0.imprint","IMPRINT",EDGE,{"disambiguationData":[TD([[subQ2,1.0]])],"derivedFrom":subQ1}),-1.0]])]});}
            var Q17;
            {var subQ0=sQuery(id+"F0.wireOp",EDGE,"E4.bottom");var subQ1=sQuery(id+"F0.wireOp",EDGE,"E1");var subQ2=makeQuery(id+"F0.imprint","INTERSECT",VERTEX,{"disambiguationData":[OD(0.0)],"derivedFrom":[subQ1,subQ0]});Q17=makeQuery(id+"F0.imprint","IMPRINT",FACE,{"disambiguationData":[TD([[makeQuery(id+"F0.imprint","IMPRINT",EDGE,{"disambiguationData":[TD([[subQ2,1.0]])],"derivedFrom":subQ1}),-1.0]])]});}
            var Q18;
            {var subQ0=sQuery(id+"F0.wireOp",EDGE,"E5.right");var subQ1=sQuery(id+"F0.wireOp",EDGE,"E5.top");var subQ2=makeQuery(id+"F0.imprint","INTERSECT",VERTEX,{"derivedFrom":[subQ1,subQ0]});Q18=makeQuery(id+"F0.imprint","IMPRINT",FACE,{"disambiguationData":[TD([[makeQuery(id+"F0.imprint","IMPRINT",EDGE,{"disambiguationData":[TD([[subQ2,1.0]])],"derivedFrom":subQ1}),1.0]])]});}
            var Q19;
            {var subQ0=sQuery(id+"F0.wireOp",EDGE,"E4.top");var subQ1=sQuery(id+"F0.wireOp",EDGE,"E2");var subQ2=makeQuery(id+"F0.imprint","INTERSECT",VERTEX,{"disambiguationData":[OD(1.0)],"derivedFrom":[subQ1,subQ0]});Q19=makeQuery(id+"F0.imprint","IMPRINT",FACE,{"disambiguationData":[TD([[makeQuery(id+"F0.imprint","IMPRINT",EDGE,{"disambiguationData":[TD([[subQ2,-1.0]])],"derivedFrom":subQ1}),-1.0]])]});}
            var Q20;
            {var subQ3=sQuery(id+"F0.wireOp",EDGE,"E4.top");var subQ6=makeQuery(id+"F0.imprint","INTERSECT",VERTEX,{"derivedFrom":[sQuery(id+"F0.wireOp",EDGE,"E2"),subQ3]});Q20=makeQuery(id+"F0.imprint","IMPRINT",FACE,{"disambiguationData":[TD([[makeQuery(id+"F0.imprint","IMPRINT",EDGE,{"disambiguationData":[TD([[subQ6,1.0]])],"derivedFrom":subQ3}),-1.0]])]});}
            var Q21;
            {var subQ0=sQuery(id+"F0.wireOp",EDGE,"E7");var subQ1=sQuery(id+"F0.wireOp",EDGE,"E4.right");var subQ2=makeQuery(id+"F0.imprint","INTERSECT",VERTEX,{"disambiguationData":[OD(0.0)],"derivedFrom":[subQ1,subQ0]});Q21=makeQuery(id+"F0.imprint","IMPRINT",FACE,{"disambiguationData":[TD([[makeQuery(id+"F0.imprint","IMPRINT",EDGE,{"disambiguationData":[TD([[subQ2,-1.0]])],"derivedFrom":subQ1}),1.0]])]});}
            var Q22;
            {var subQ0=sQuery(id+"F0.wireOp",EDGE,"E7");var subQ1=sQuery(id+"F0.wireOp",EDGE,"E1");var subQ2=makeQuery(id+"F0.imprint","INTERSECT",VERTEX,{"disambiguationData":[OD(0.0)],"derivedFrom":[subQ1,subQ0]});Q22=makeQuery(id+"F0.imprint","IMPRINT",FACE,{"disambiguationData":[TD([[makeQuery(id+"F0.imprint","IMPRINT",EDGE,{"disambiguationData":[TD([[subQ2,1.0]])],"derivedFrom":subQ1}),1.0]])]});}
            var Q23;
            {var subQ0=sQuery(id+"F0.wireOp",EDGE,"E7");var subQ1=sQuery(id+"F0.wireOp",EDGE,"E1");var subQ2=makeQuery(id+"F0.imprint","INTERSECT",VERTEX,{"disambiguationData":[OD(0.0)],"derivedFrom":[subQ1,subQ0]});Q23=makeQuery(id+"F0.imprint","IMPRINT",FACE,{"disambiguationData":[TD([[makeQuery(id+"F0.imprint","IMPRINT",EDGE,{"disambiguationData":[TD([[subQ2,1.0]])],"derivedFrom":subQ1}),-1.0]])]});}
            var Q24;
            {var subQ0=sQuery(id+"F0.wireOp",EDGE,"E4.right");var subQ1=sQuery(id+"F0.wireOp",EDGE,"E1");var subQ2=makeQuery(id+"F0.imprint","INTERSECT",VERTEX,{"derivedFrom":[subQ1,subQ0]});Q24=makeQuery(id+"F0.imprint","IMPRINT",FACE,{"disambiguationData":[TD([[makeQuery(id+"F0.imprint","IMPRINT",EDGE,{"disambiguationData":[TD([[subQ2,1.0]])],"derivedFrom":subQ1}),-1.0]])]});}
            var Q25;
            Q25=makeQuery(id+"F0.imprint","IMPRINT",FACE,{"disambiguationData":[TD([[makeQuery(id+"F0.imprint","IMPRINT",EDGE,{"derivedFrom":sQuery(id+"F0.wireOp",EDGE,"E6.right")}),-1.0]])]});
            var Q26;
            {var subQ0=sQuery(id+"F0.wireOp",EDGE,"E4.right");var subQ1=sQuery(id+"F0.wireOp",EDGE,"E2");var subQ2=makeQuery(id+"F0.imprint","INTERSECT",VERTEX,{"derivedFrom":[subQ1,subQ0]});Q26=makeQuery(id+"F0.imprint","IMPRINT",FACE,{"disambiguationData":[TD([[makeQuery(id+"F0.imprint","IMPRINT",EDGE,{"disambiguationData":[TD([[subQ2,1.0]])],"derivedFrom":subQ1}),-1.0]])]});}
            var Q27;
            {var subQ0=sQuery(id+"F0.wireOp",EDGE,"E7");var subQ1=sQuery(id+"F0.wireOp",EDGE,"E2");var subQ2=makeQuery(id+"F0.imprint","INTERSECT",VERTEX,{"disambiguationData":[OD(0.0)],"derivedFrom":[subQ1,subQ0]});Q27=makeQuery(id+"F0.imprint","IMPRINT",FACE,{"disambiguationData":[TD([[makeQuery(id+"F0.imprint","IMPRINT",EDGE,{"disambiguationData":[TD([[subQ2,1.0]])],"derivedFrom":subQ1}),1.0]])]});}
            var Q28;
            {var subQ0=sQuery(id+"F0.wireOp",EDGE,"E7");var subQ1=sQuery(id+"F0.wireOp",EDGE,"E2");var subQ2=makeQuery(id+"F0.imprint","INTERSECT",VERTEX,{"disambiguationData":[OD(0.0)],"derivedFrom":[subQ1,subQ0]});Q28=makeQuery(id+"F0.imprint","IMPRINT",FACE,{"disambiguationData":[TD([[makeQuery(id+"F0.imprint","IMPRINT",EDGE,{"disambiguationData":[TD([[subQ2,1.0]])],"derivedFrom":subQ1}),-1.0]])]});}
            var Q29;
            {var subQ0=sQuery(id+"F0.wireOp",EDGE,"E7");var subQ1=sQuery(id+"F0.wireOp",EDGE,"E3");var subQ2=makeQuery(id+"F0.imprint","INTERSECT",VERTEX,{"disambiguationData":[OD(1.0)],"derivedFrom":[subQ1,subQ0]});Q29=makeQuery(id+"F0.imprint","IMPRINT",FACE,{"disambiguationData":[TD([[makeQuery(id+"F0.imprint","IMPRINT",EDGE,{"disambiguationData":[TD([[subQ2,1.0]])],"derivedFrom":subQ1}),-1.0]])]});}
            var Q30;
            {var subQ0=sQuery(id+"F0.wireOp",EDGE,"E4.left");var subQ1=sQuery(id+"F0.wireOp",EDGE,"E0");var subQ2=makeQuery(id+"F0.imprint","INTERSECT",VERTEX,{"derivedFrom":[subQ1,subQ0]});Q30=makeQuery(id+"F0.imprint","IMPRINT",FACE,{"disambiguationData":[TD([[makeQuery(id+"F0.imprint","IMPRINT",EDGE,{"disambiguationData":[TD([[subQ2,-1.0]])],"derivedFrom":subQ1}),-1.0]])]});}
            var Q31;
            {var subQ0=sQuery(id+"F0.wireOp",EDGE,"E7");var subQ1=sQuery(id+"F0.wireOp",EDGE,"E3");var subQ2=makeQuery(id+"F0.imprint","INTERSECT",VERTEX,{"disambiguationData":[OD(0.0)],"derivedFrom":[subQ1,subQ0]});Q31=makeQuery(id+"F0.imprint","IMPRINT",FACE,{"disambiguationData":[TD([[makeQuery(id+"F0.imprint","IMPRINT",EDGE,{"disambiguationData":[TD([[subQ2,1.0]])],"derivedFrom":subQ1}),1.0]])]});}
            var Q32;
            {var subQ0=sQuery(id+"F0.wireOp",EDGE,"E7");var subQ1=sQuery(id+"F0.wireOp",EDGE,"E0");var subQ2=makeQuery(id+"F0.imprint","INTERSECT",VERTEX,{"disambiguationData":[OD(0.0)],"derivedFrom":[subQ1,subQ0]});Q32=makeQuery(id+"F0.imprint","IMPRINT",FACE,{"disambiguationData":[TD([[makeQuery(id+"F0.imprint","IMPRINT",EDGE,{"disambiguationData":[TD([[subQ2,-1.0]])],"derivedFrom":subQ1}),1.0]])]});}
            extrude(context, id + "F2", {"entities" : qUnion([Q0, Q1, Q2, Q3, Q4, Q5, Q6, Q7, Q8, Q9, Q10, Q11, Q12, Q13, Q14, Q15, Q16, Q17, Q18, Q19, Q20, Q21, Q22, Q23, Q24, Q25, Q26, Q27, Q28, Q29, Q30, Q31, Q32]), "operationType" : NewBodyOperationType.ADD, "depth" : 12 * mm});
        }
        {
            var Q0;
            Q0=makeQuery(id+"F2.opExtrude","CAP_FACE",FACE,{"disambiguationData":[OSD([sQuery(id+"F0.wireOp",EDGE,"E6.bottom"),sQuery(id+"F0.wireOp",EDGE,"E6.top"),sQuery(id+"F0.wireOp",EDGE,"E6.left"),sQuery(id+"F0.wireOp",EDGE,"E6.right"),sQuery(id+"F0.wireOp",EDGE,"E8.filletArc"),sQuery(id+"F0.wireOp",EDGE,"E9.filletArc"),sQuery(id+"F0.wireOp",EDGE,"E10.filletArc"),sQuery(id+"F0.wireOp",EDGE,"E11.filletArc")])],"isStart":false});
            shell(context, id + "F3", {"entities" : qUnion([Q0]), "thickness" : 2 * mm});
        }
        {
            var Q0;
            {var subQ0=sQuery(id+"F0.wireOp",EDGE,"E7");var subQ7=sQuery(id+"F0.wireOp",EDGE,"E5.bottom");var subQ12=makeQuery(id+"F0.imprint","INTERSECT",VERTEX,{"disambiguationData":[OD(0.0)],"derivedFrom":[subQ7,subQ0]});Q0=makeQuery(id+"F0.imprint","IMPRINT",FACE,{"disambiguationData":[TD([[makeQuery(id+"F0.imprint","IMPRINT",EDGE,{"disambiguationData":[TD([[subQ12,-1.0]])],"derivedFrom":subQ7}),-1.0]])]});}
            var sketch = newSketch(context, id + "F4", { "sketchPlane" : qUnion([Q0])});
            skCircle(sketch, "E12", {"center": v(0, 0) * mm, "radius": 12.5 * mm});
            skCircle(sketch, "E13", {"center": v(0, 0) * mm, "radius": 38.1 * mm, "construction": true});
            skCircle(sketch, "E14", {"center": v(38.1, 0) * mm, "radius": 2 * mm});
            skCircle(sketch, "E15", {"center": v(-38.1, 0) * mm, "radius": 2 * mm});
            skSolve(sketch);
        }
        {
            var Q0;
            {var subQ0=sQuery(id+"F4.wireOp",EDGE,"E14");var subQ1=sQuery(id+"F0.wireOp",EDGE,"E7");var subQ2=sQuery(id+"F0.wireOp",EDGE,"E5.right");var subQ3=makeQuery(id+"F0.imprint","IMPRINT",EDGE,{"disambiguationData":[TD([[makeQuery(id+"F0.imprint","INTERSECT",VERTEX,{"disambiguationData":[OD(0.0)],"derivedFrom":[subQ2,subQ1]}),-1.0]])],"derivedFrom":subQ2});var subQ4=makeQuery(id+"F4.imprint","INTERSECT",VERTEX,{"disambiguationData":[OD(0.0)],"derivedFrom":[subQ3,subQ0]});Q0=makeQuery(id+"F4.imprint","IMPRINT",FACE,{"disambiguationData":[TD([[makeQuery(id+"F4.imprint","IMPRINT",EDGE,{"disambiguationData":[TD([[subQ4,1.0]])],"derivedFrom":subQ0}),1.0]])]});}
            var Q1;
            {var subQ0=sQuery(id+"F4.wireOp",EDGE,"E14");var subQ1=sQuery(id+"F0.wireOp",EDGE,"E7");var subQ2=sQuery(id+"F0.wireOp",EDGE,"E5.right");var subQ3=makeQuery(id+"F0.imprint","IMPRINT",EDGE,{"disambiguationData":[TD([[makeQuery(id+"F0.imprint","INTERSECT",VERTEX,{"disambiguationData":[OD(0.0)],"derivedFrom":[subQ2,subQ1]}),-1.0]])],"derivedFrom":subQ2});var subQ4=makeQuery(id+"F4.imprint","INTERSECT",VERTEX,{"disambiguationData":[OD(0.0)],"derivedFrom":[subQ3,subQ0]});Q1=makeQuery(id+"F4.imprint","IMPRINT",FACE,{"disambiguationData":[TD([[makeQuery(id+"F4.imprint","IMPRINT",EDGE,{"disambiguationData":[TD([[subQ4,-1.0]])],"derivedFrom":subQ0}),1.0]])]});}
            var Q2;
            Q2=makeQuery(id+"F4.imprint","IMPRINT",FACE,{"disambiguationData":[TD([[makeQuery(id+"F4.imprint","IMPRINT",EDGE,{"derivedFrom":sQuery(id+"F4.wireOp",EDGE,"E12")}),1.0]])]});
            var Q3;
            {var subQ0=sQuery(id+"F4.wireOp",EDGE,"E15");var subQ1=sQuery(id+"F0.wireOp",EDGE,"E7");var subQ2=sQuery(id+"F0.wireOp",EDGE,"E5.left");var subQ3=makeQuery(id+"F0.imprint","IMPRINT",EDGE,{"disambiguationData":[TD([[makeQuery(id+"F0.imprint","INTERSECT",VERTEX,{"disambiguationData":[OD(0.0)],"derivedFrom":[subQ2,subQ1]}),-1.0]])],"derivedFrom":subQ2});var subQ4=makeQuery(id+"F4.imprint","INTERSECT",VERTEX,{"disambiguationData":[OD(0.0)],"derivedFrom":[subQ3,subQ0]});Q3=makeQuery(id+"F4.imprint","IMPRINT",FACE,{"disambiguationData":[TD([[makeQuery(id+"F4.imprint","IMPRINT",EDGE,{"disambiguationData":[TD([[subQ4,1.0]])],"derivedFrom":subQ0}),1.0]])]});}
            var Q4;
            {var subQ0=sQuery(id+"F4.wireOp",EDGE,"E15");var subQ1=sQuery(id+"F0.wireOp",EDGE,"E7");var subQ2=sQuery(id+"F0.wireOp",EDGE,"E5.left");var subQ3=makeQuery(id+"F0.imprint","IMPRINT",EDGE,{"disambiguationData":[TD([[makeQuery(id+"F0.imprint","INTERSECT",VERTEX,{"disambiguationData":[OD(0.0)],"derivedFrom":[subQ2,subQ1]}),-1.0]])],"derivedFrom":subQ2});var subQ4=makeQuery(id+"F4.imprint","INTERSECT",VERTEX,{"disambiguationData":[OD(0.0)],"derivedFrom":[subQ3,subQ0]});Q4=makeQuery(id+"F4.imprint","IMPRINT",FACE,{"disambiguationData":[TD([[makeQuery(id+"F4.imprint","IMPRINT",EDGE,{"disambiguationData":[TD([[subQ4,-1.0]])],"derivedFrom":subQ0}),1.0]])]});}
            extrude(context, id + "F5", {"entities" : qUnion([Q0, Q1, Q2, Q3, Q4]), "operationType" : NewBodyOperationType.REMOVE, "endBound" : BoundingType.THROUGH_ALL, "oppositeDirection" : true, "depth" : 25 * mm});
        }
        {
            var Q0;
            {var subQ0=sQuery(id+"F0.wireOp",EDGE,"E6.top");Q0=makeQuery(id+"F2.boolean.opBoolean","MERGE",FACE,{"derivedFrom":[makeQuery(id+"F1.opExtrude","SWEPT_FACE",FACE,{"disambiguationData":[OSD([subQ0]),TDD([makeQuery(id+"F0.imprint","IMPRINT",EDGE,{"disambiguationData":[TD([[makeQuery(id+"F0.imprint","INTERSECT",VERTEX,{"derivedFrom":[subQ0,sQuery(id+"F0.wireOp",EDGE,"E10.filletArc")]}),-1.0]])],"derivedFrom":subQ0})])]}),makeQuery(id+"F1.opExtrude","SWEPT_FACE",FACE,{"disambiguationData":[OSD([subQ0]),TDD([makeQuery(id+"F0.imprint","IMPRINT",EDGE,{"disambiguationData":[TD([[makeQuery(id+"F0.imprint","INTERSECT",VERTEX,{"derivedFrom":[subQ0,sQuery(id+"F0.wireOp",EDGE,"E11.filletArc")]}),1.0]])],"derivedFrom":subQ0})])]}),makeQuery(id+"F2.opExtrude","SWEPT_FACE",FACE,{"disambiguationData":[OSD([subQ0])]})]});}
            var sketch = newSketch(context, id + "F6", { "sketchPlane" : qUnion([Q0])});
            skLineSegment(sketch, "E16", {"start": v(-35.8, 2.88) * mm, "end": v(37.37, 3) * mm, "construction": true});
            skCircle(sketch, "E17", {"center": v(10, 2.96) * mm, "radius": 2.5 * mm});
            skCircle(sketch, "E18", {"center": v(-10, 2.92) * mm, "radius": 2.5 * mm});
            skPoint(sketch, "E19.0", {"position": v(-35.8, -2) * mm});
            skPoint(sketch, "E19.1", {"position": v(37.37, -2) * mm});
            skPoint(sketch, "E20", {"position": v(0, 2.94) * mm});
            skCircle(sketch, "E21", {"center": v(0, 2.94) * mm, "radius": 2.5 * mm});
            skSolve(sketch);
        }
        {
            var Q0;
            Q0=makeQuery(id+"F6.imprint","IMPRINT",FACE,{"disambiguationData":[TD([[makeQuery(id+"F6.imprint","IMPRINT",EDGE,{"derivedFrom":sQuery(id+"F6.wireOp",EDGE,"E18")}),1.0]])]});
            var Q1;
            Q1=makeQuery(id+"F6.imprint","IMPRINT",FACE,{"disambiguationData":[TD([[makeQuery(id+"F6.imprint","IMPRINT",EDGE,{"derivedFrom":sQuery(id+"F6.wireOp",EDGE,"E21")}),1.0]])]});
            var Q2;
            Q2=makeQuery(id+"F6.imprint","IMPRINT",FACE,{"disambiguationData":[TD([[makeQuery(id+"F6.imprint","IMPRINT",EDGE,{"derivedFrom":sQuery(id+"F6.wireOp",EDGE,"E17")}),1.0]])]});
            extrude(context, id + "F7", {"entities" : qUnion([Q0, Q1, Q2]), "operationType" : NewBodyOperationType.REMOVE, "endBound" : BoundingType.UP_TO_NEXT, "oppositeDirection" : true, "depth" : 25 * mm, "offsetDistance" : 25 * mm});
        }
        {
            var Q0;
            {var subQ0=sQuery(id+"F0.wireOp",EDGE,"E6.left");Q0=makeQuery(id+"F2.boolean.opBoolean","MERGE",FACE,{"derivedFrom":[makeQuery(id+"F1.opExtrude","SWEPT_FACE",FACE,{"disambiguationData":[OSD([subQ0])]}),makeQuery(id+"F2.opExtrude","SWEPT_FACE",FACE,{"disambiguationData":[OSD([subQ0])]})]});}
            var sketch = newSketch(context, id + "F8", { "sketchPlane" : qUnion([Q0])});
            skLineSegment(sketch, "E22", {"start": v(-14.83, 3) * mm, "end": v(16.77, 3) * mm, "construction": true});
            skCircle(sketch, "E23", {"center": v(-14.83, 3) * mm, "radius": 2.5 * mm});
            skCircle(sketch, "E24", {"center": v(-7.83, 3) * mm, "radius": 2.5 * mm});
            skCircle(sketch, "E25", {"center": v(-0.83, 3) * mm, "radius": 2.5 * mm});
            skPoint(sketch, "E26.0", {"position": v(1.23, -2) * mm});
            skSolve(sketch);
        }
        {
            var Q0;
            Q0=makeQuery(id+"F8.imprint","IMPRINT",FACE,{"disambiguationData":[TD([[makeQuery(id+"F8.imprint","IMPRINT",EDGE,{"derivedFrom":sQuery(id+"F8.wireOp",EDGE,"E23")}),1.0]])]});
            var Q1;
            Q1=makeQuery(id+"F8.imprint","IMPRINT",FACE,{"disambiguationData":[TD([[makeQuery(id+"F8.imprint","IMPRINT",EDGE,{"derivedFrom":sQuery(id+"F8.wireOp",EDGE,"E24")}),1.0]])]});
            var Q2;
            Q2=makeQuery(id+"F8.imprint","IMPRINT",FACE,{"disambiguationData":[TD([[makeQuery(id+"F8.imprint","IMPRINT",EDGE,{"derivedFrom":sQuery(id+"F8.wireOp",EDGE,"E25")}),1.0]])]});
            extrude(context, id + "F9", {"entities" : qUnion([Q0, Q1, Q2]), "operationType" : NewBodyOperationType.REMOVE, "endBound" : BoundingType.THROUGH_ALL, "oppositeDirection" : true, "depth" : 25 * mm, "offsetDistance" : 25 * mm});
        }
        {
            var Q0;
            {var subQ0=sQuery(id+"F0.wireOp",EDGE,"E7");var subQ1=sQuery(id+"F0.wireOp",EDGE,"E6.top");Q0=makeQuery(id+"F1.opExtrude","CAP_EDGE",EDGE,{"disambiguationData":[OSD([subQ0]),TDD([makeQuery(id+"F0.imprint","IMPRINT",EDGE,{"disambiguationData":[TD([[makeQuery(id+"F0.imprint","INTERSECT",VERTEX,{"disambiguationData":[OD(0.0)],"derivedFrom":[subQ1,subQ0]}),-1.0]])],"derivedFrom":subQ0})])],"isStart":true});}
            var Q1;
            {var subQ0=sQuery(id+"F0.wireOp",EDGE,"E7");var subQ1=sQuery(id+"F0.wireOp",EDGE,"E6.bottom");Q1=makeQuery(id+"F1.opExtrude","CAP_EDGE",EDGE,{"disambiguationData":[OSD([subQ0]),TDD([makeQuery(id+"F0.imprint","IMPRINT",EDGE,{"disambiguationData":[TD([[makeQuery(id+"F0.imprint","INTERSECT",VERTEX,{"disambiguationData":[OD(0.0)],"derivedFrom":[subQ1,subQ0]}),1.0]])],"derivedFrom":subQ0})])],"isStart":true});}
            fillet(context, id + "F10", {"entities" : qUnion([Q0, Q1]), "radius" : 1.5 * mm, "tangentPropagation" : true, "allowEdgeOverflow" : false});
        }
    });
